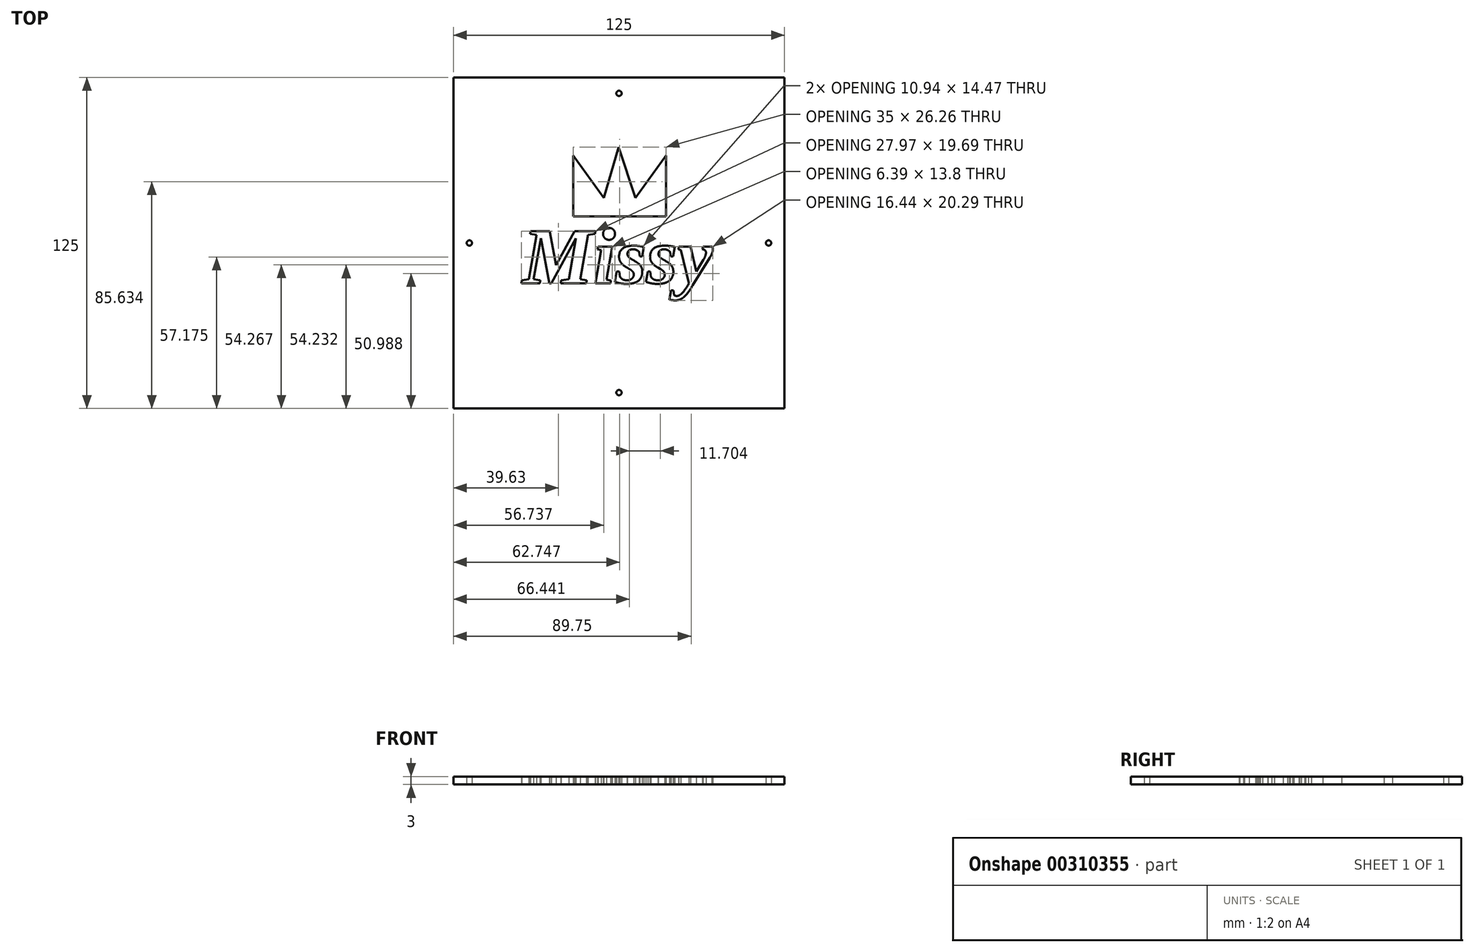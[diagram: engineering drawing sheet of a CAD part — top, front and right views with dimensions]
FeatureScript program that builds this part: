
annotation { "Feature Type Name" : "Feature", "Feature Type Description" : "" }
export const myFeature = defineFeature(function(context is Context, id is Id, definition is map)
    precondition{}
    {
        {
            var Q0;
            Q0=qCreatedBy(makeId("Top.planeOp"),FACE);
            var sketch = newSketch(context, id + "F0", { "sketchPlane" : qUnion([Q0])});
            skLineSegment(sketch, "E0.bottom", {"start": v(-379.03, 200.6) * mm, "end": v(-254.03, 200.6) * mm});
            skLineSegment(sketch, "E0.top", {"start": v(-379.03, 75.6) * mm, "end": v(-254.03, 75.6) * mm});
            skLineSegment(sketch, "E0.left", {"start": v(-379.03, 200.6) * mm, "end": v(-379.03, 75.6) * mm});
            skLineSegment(sketch, "E0.right", {"start": v(-254.03, 200.6) * mm, "end": v(-254.03, 75.6) * mm});
            skCircle(sketch, "E1", {"center": v(-260.03, 138.1) * mm, "radius": 1 * mm});
            skCircle(sketch, "E2", {"center": v(-316.53, 81.6) * mm, "radius": 1 * mm});
            skCircle(sketch, "E3", {"center": v(-373.03, 138.1) * mm, "radius": 1 * mm});
            skCircle(sketch, "E4", {"center": v(-316.53, 194.6) * mm, "radius": 1 * mm});
            skText(sketch, "E5", { "text": "Missy", "fontName": "Tinos-BoldItalic.ttf"});
            skLineSegment(sketch, "E6", {"start": v(-333.78, 148.12) * mm, "end": v(-298.78, 148.12) * mm});
            skLineSegment(sketch, "E7", {"start": v(-333.78, 148.12) * mm, "end": v(-333.78, 171.12) * mm});
            skLineSegment(sketch, "E8", {"start": v(-298.78, 148.12) * mm, "end": v(-298.78, 171.12) * mm});
            skLineSegment(sketch, "E9", {"start": v(-319.17, 174.37) * mm, "end": v(-314.17, 174.37) * mm});
            skLineSegment(sketch, "E10", {"start": v(-316.67, 174.37) * mm, "end": v(-322.28, 155.2) * mm});
            skLineSegment(sketch, "E11", {"start": v(-316.67, 174.37) * mm, "end": v(-310.29, 155.2) * mm});
            skLineSegment(sketch, "E12", {"start": v(-322.28, 155.2) * mm, "end": v(-333.78, 171.12) * mm});
            skLineSegment(sketch, "E13", {"start": v(-310.29, 155.2) * mm, "end": v(-298.78, 171.12) * mm});
            const initialGuessF0  = {"E5": [-0.35299, 0.12294, 1, 0, 0.02165]};
            skSetInitialGuess(sketch, initialGuessF0);
            skSolve(sketch);
        }
        {
            var Q0;
            Q0 = qSketchRegion(id + "F0", true);
            var Q1;
            Q1=makeQuery(id+"F0.imprint","IMPRINT",FACE,{"disambiguationData":[TD([[makeQuery(id+"F0.imprint","IMPRINT",EDGE,{"derivedFrom":sQuery(id+"F0.wireOp",EDGE,"E0.bottom")}),-1.0]])]});
            extrude(context, id + "F1", {"entities" : qUnion([Q0, Q1]), "depth" : 3 * mm});
        }
    });
